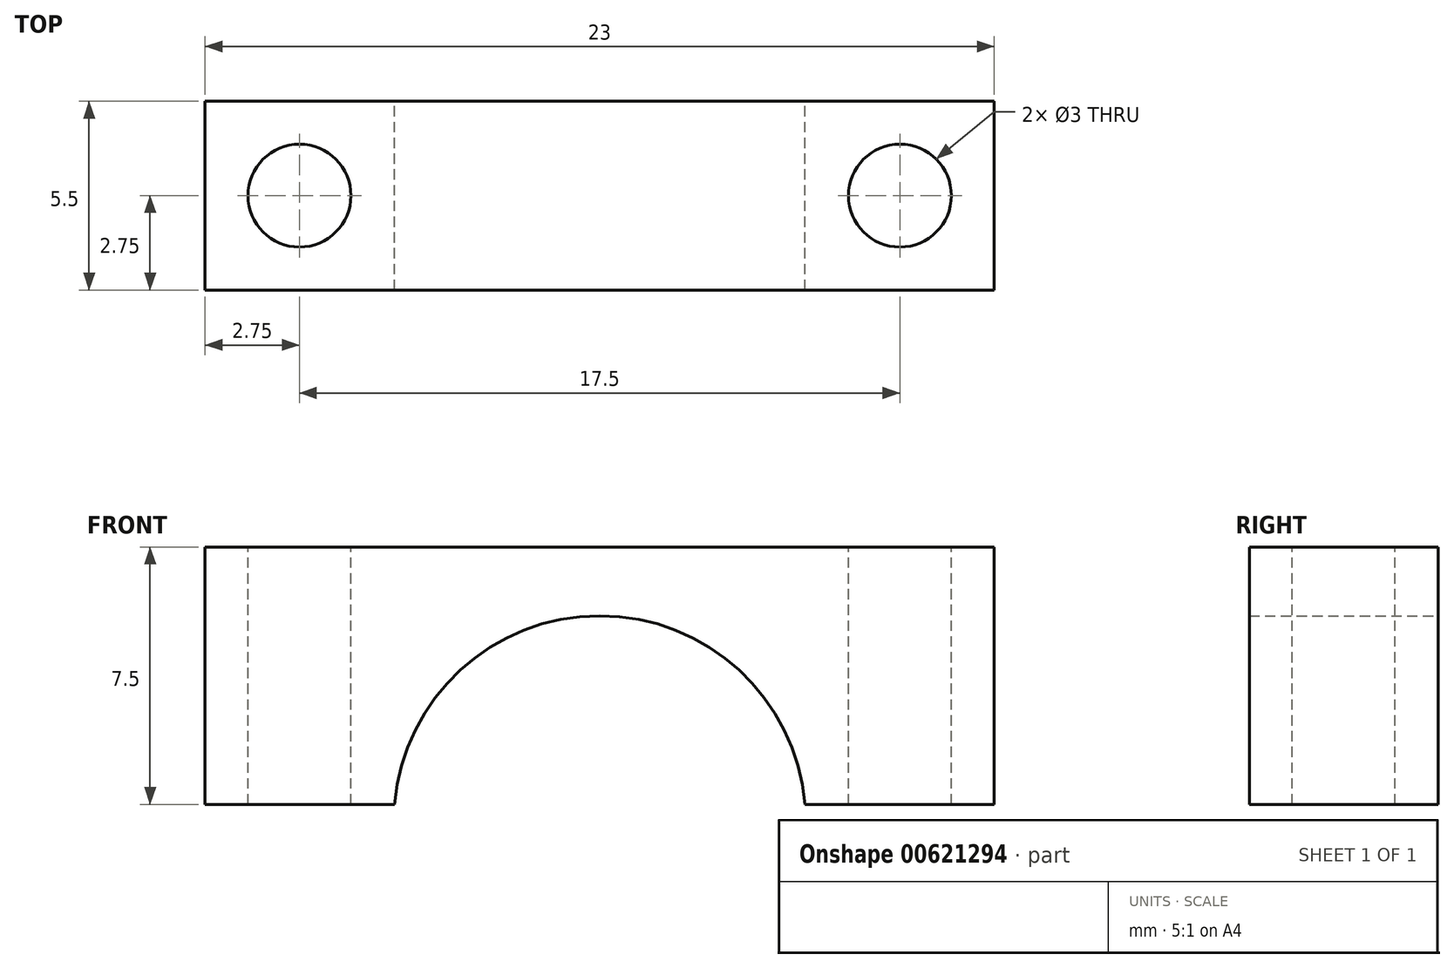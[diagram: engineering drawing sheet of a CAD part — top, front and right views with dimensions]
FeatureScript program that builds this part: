
annotation { "Feature Type Name" : "Feature", "Feature Type Description" : "" }
export const myFeature = defineFeature(function(context is Context, id is Id, definition is map)
    precondition{}
    {
        {
            assignVariable(context, id + "F0", {"name" : "Ds", "anyValue" : 2.5});
        }
        {
            var Q0;
            Q0=qCreatedBy(makeId("Front.planeOp"),FACE);
            var sketch = newSketch(context, id + "F1", { "sketchPlane" : qUnion([Q0])});
            skCircle(sketch, "E0", {"center": v(0, 0) * mm, "radius": 6 * mm});
            skLineSegment(sketch, "E1.bottom", {"start": v(11.5, 8) * mm, "end": v(-11.5, 8) * mm});
            skLineSegment(sketch, "E1.top", {"start": v(11.5, -8) * mm, "end": v(-11.5, -8) * mm, "construction": true});
            skLineSegment(sketch, "E1.left", {"start": v(11.5, 8) * mm, "end": v(11.5, -8) * mm, "construction": true});
            skLineSegment(sketch, "E1.right", {"start": v(-11.5, 8) * mm, "end": v(-11.5, -8) * mm, "construction": true});
            skLineSegment(sketch, "E2.bottom", {"start": v(-10, 0) * mm, "end": v(-7.5, 0) * mm, "construction": true});
            skLineSegment(sketch, "E2.top", {"start": v(-10, 9.89) * mm, "end": v(-7.5, 9.89) * mm, "construction": true});
            skLineSegment(sketch, "E2.left", {"start": v(-10, 0) * mm, "end": v(-10, 9.89) * mm, "construction": true});
            skLineSegment(sketch, "E2.right", {"start": v(-7.5, 0) * mm, "end": v(-7.5, 9.89) * mm, "construction": true});
            skLineSegment(sketch, "E3", {"start": v(-11.5, 0.5) * mm, "end": v(11.5, 0.5) * mm});
            skLineSegment(sketch, "E4", {"start": v(-11.5, 8) * mm, "end": v(-11.5, 0.5) * mm});
            skLineSegment(sketch, "E5", {"start": v(11.5, 8) * mm, "end": v(11.5, 0.5) * mm});
            skSolve(sketch);
        }
        {
            var Q0;
            Q0=makeQuery(id+"F1.imprint","IMPRINT",FACE,{"disambiguationData":[TD([[makeQuery(id+"F1.imprint","IMPRINT",EDGE,{"derivedFrom":sQuery(id+"F1.wireOp",EDGE,"E1.bottom")}),1.0]])]});
            extrude(context, id + "F2", {"entities" : qUnion([Q0]), "endBound" : BoundingType.SYMMETRIC, "depth" : (getVariable(context, 'Ds') + 3) * mm, "offsetDistance" : 25 * mm});
        }
        {
            var Q0;
            Q0=makeQuery(id+"F2.opExtrude","SWEPT_FACE",FACE,{"disambiguationData":[OSD([sQuery(id+"F1.wireOp",EDGE,"E1.bottom")])]});
            var sketch = newSketch(context, id + "F3", { "sketchPlane" : qUnion([Q0])});
            skCircle(sketch, "E6", {"center": v(-8.75, 0) * mm, "radius": 1.6 * mm, "construction": true});
            skLineSegment(sketch, "E7", {"start": v(-8.75, 0) * mm, "end": v(0, 0) * mm, "construction": true});
            skCircle(sketch, "E8.MirrorC", {"center": v(8.75, 0) * mm, "radius": 1.6 * mm, "construction": true});
            skSolve(sketch);
        }
        {
            var Q0;
            Q0=sQuery(id+"F3.wireOp",VERTEX,"E6.center");
            var Q1;
            Q1=sQuery(id+"F3.wireOp",VERTEX,"E8.MirrorC.center");
            var Q2;
            Q2=makeQuery(id+"F2.opExtrude","SWEPT_BODY",BODY,{"disambiguationData":[OSD([sQuery(id+"F1.wireOp",EDGE,"E0"),sQuery(id+"F1.wireOp",EDGE,"E1.bottom"),sQuery(id+"F1.wireOp",EDGE,"E3"),sQuery(id+"F1.wireOp",EDGE,"E4"),sQuery(id+"F1.wireOp",EDGE,"E5")])]});
            hole(context, id + "F4", {"style" : HoleStyle.SIMPLE, "endStyle" : HoleEndStyle.THROUGH, "standardTappedOrClearance" : lookupTablePath({ "standard" : "ISO", "size" : "3", "type" : "Drilled" }), "standardBlindInLast" : lookupTablePath({ "standard" : "ISO", "size" : "3", "type" : "Drilled" }), "holeDiameter" : 3 * mm, "majorDiameter" : 5 * mm, "isTappedThrough" : true, "tappedDepth" : 12 * mm, "tapClearance" : 3, "locations" : qUnion([Q0, Q1]), "scope" : qUnion([Q2])});
        }
    });
